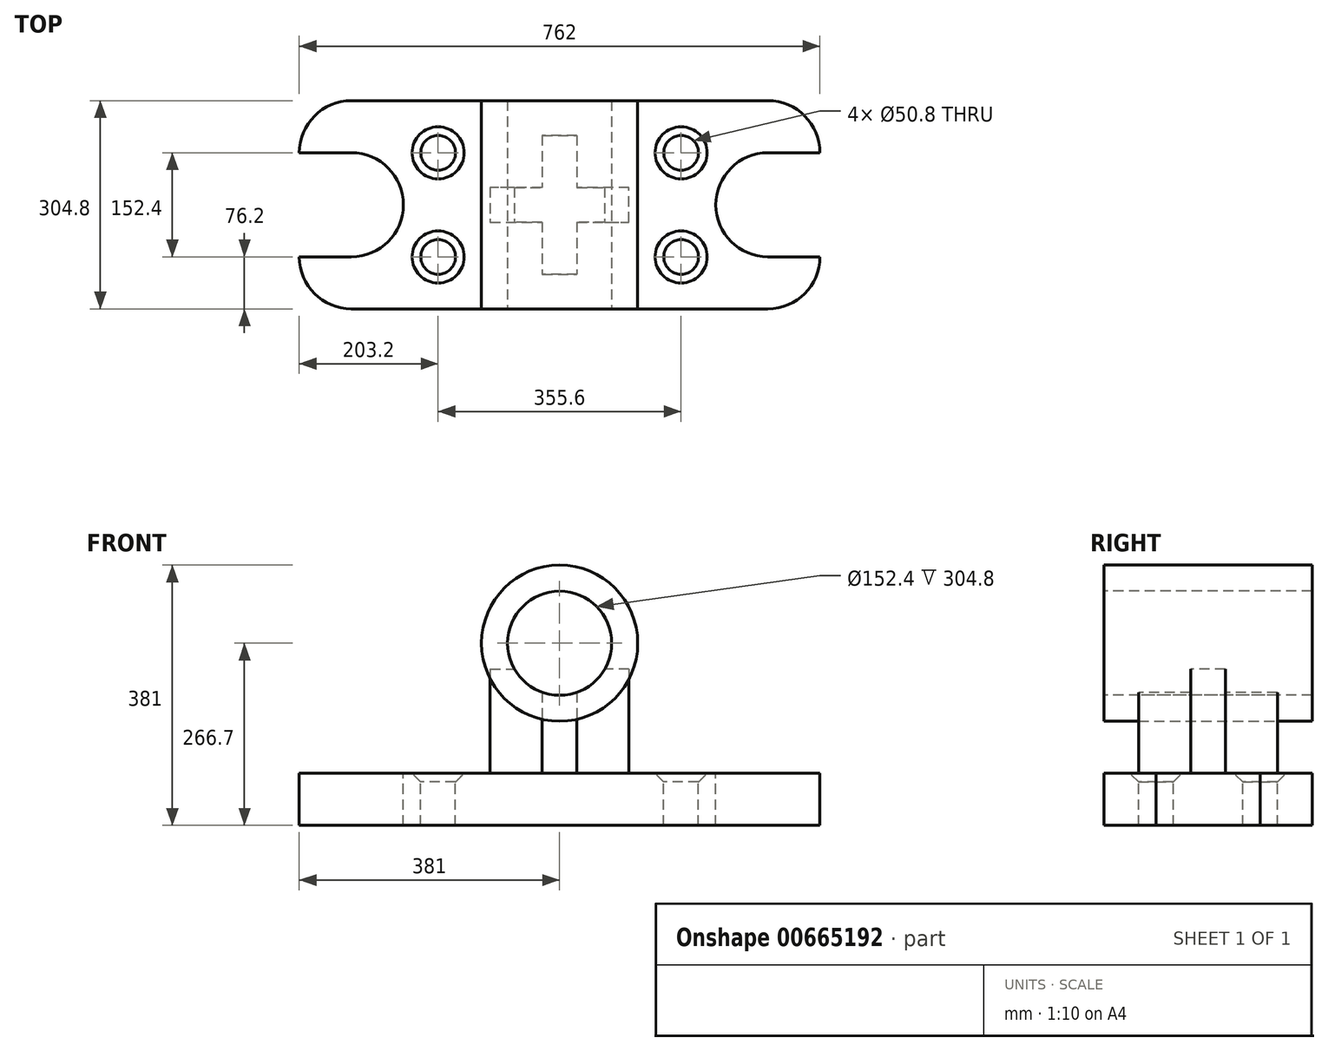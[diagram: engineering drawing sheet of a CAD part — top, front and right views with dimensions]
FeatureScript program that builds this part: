
annotation { "Feature Type Name" : "Feature", "Feature Type Description" : "" }
export const myFeature = defineFeature(function(context is Context, id is Id, definition is map)
    precondition{}
    {
        {
            var Q0;
            Q0=qCreatedBy(makeId("Top.planeOp"),FACE);
            var sketch = newSketch(context, id + "F0", { "sketchPlane" : qUnion([Q0])});
            skLineSegment(sketch, "E0.bottom", {"start": v(76.2, 0) * mm, "end": v(685.8, 0) * mm});
            skLineSegment(sketch, "E0.top", {"start": v(76.2, 304.8) * mm, "end": v(685.8, 304.8) * mm});
            skLineSegment(sketch, "E0.left", {"start": v(0, 76.2) * mm, "end": v(0, 228.6) * mm});
            skLineSegment(sketch, "E0.right", {"start": v(762, 76.2) * mm, "end": v(762, 228.6) * mm});
            skLineSegment(sketch, "E1", {"start": v(0, 228.6) * mm, "end": v(76.2, 228.6) * mm});
            skLineSegment(sketch, "E2", {"start": v(0, 76.2) * mm, "end": v(76.2, 76.2) * mm});
            skArc(sketch, "E3", {"start": v(76.2, 76.2) * mm, "mid": v(152.4, 152.4) * mm, "end": v(76.2, 228.6) * mm});
            skLineSegment(sketch, "E4", {"start": v(762, 228.6) * mm, "end": v(685.8, 228.6) * mm});
            skLineSegment(sketch, "E5", {"start": v(762, 76.2) * mm, "end": v(685.8, 76.2) * mm});
            skArc(sketch, "E6", {"start": v(685.8, 228.6) * mm, "mid": v(609.6, 152.4) * mm, "end": v(685.8, 76.2) * mm});
            skPoint(sketch, "E7.visualSharp", {"position": v(0, 304.8) * mm});
            skArc(sketch, "E7.filletArc", {"start": v(76.2, 304.8) * mm, "mid": v(22.32, 282.48) * mm, "end": v(0, 228.6) * mm});
            skPoint(sketch, "E8.visualSharp", {"position": v(762, 304.8) * mm});
            skArc(sketch, "E8.filletArc", {"start": v(762, 228.6) * mm, "mid": v(739.68, 282.48) * mm, "end": v(685.8, 304.8) * mm});
            skPoint(sketch, "E9.visualSharp", {"position": v(762, 0) * mm});
            skArc(sketch, "E9.filletArc", {"start": v(685.8, 0) * mm, "mid": v(739.68, 22.32) * mm, "end": v(762, 76.2) * mm});
            skPoint(sketch, "E10.visualSharp", {"position": v(0, 0) * mm});
            skArc(sketch, "E10.filletArc", {"start": v(0, 76.2) * mm, "mid": v(22.32, 22.32) * mm, "end": v(76.2, 0) * mm});
            skCircle(sketch, "E11", {"center": v(203.2, 228.6) * mm, "radius": 38.1 * mm});
            skCircle(sketch, "E12", {"center": v(203.2, 228.6) * mm, "radius": 25.4 * mm});
            skCircle(sketch, "E13", {"center": v(203.2, 76.2) * mm, "radius": 38.1 * mm});
            skCircle(sketch, "E14", {"center": v(203.2, 76.2) * mm, "radius": 25.4 * mm});
            skCircle(sketch, "E15", {"center": v(558.8, 76.2) * mm, "radius": 38.1 * mm});
            skCircle(sketch, "E16", {"center": v(558.8, 76.2) * mm, "radius": 25.4 * mm});
            skCircle(sketch, "E17", {"center": v(558.8, 228.6) * mm, "radius": 38.1 * mm});
            skCircle(sketch, "E18", {"center": v(558.8, 228.6) * mm, "radius": 25.4 * mm});
            skLineSegment(sketch, "E19", {"start": v(279.4, 177.8) * mm, "end": v(279.4, 127) * mm});
            skLineSegment(sketch, "E20", {"start": v(279.4, 127) * mm, "end": v(355.6, 127) * mm});
            skLineSegment(sketch, "E21", {"start": v(355.6, 127) * mm, "end": v(355.6, 50.8) * mm});
            skLineSegment(sketch, "E22", {"start": v(355.6, 50.8) * mm, "end": v(406.4, 50.8) * mm});
            skLineSegment(sketch, "E23", {"start": v(406.4, 50.8) * mm, "end": v(406.4, 127) * mm});
            skLineSegment(sketch, "E24", {"start": v(406.4, 127) * mm, "end": v(482.6, 127) * mm});
            skLineSegment(sketch, "E25", {"start": v(482.6, 127) * mm, "end": v(482.6, 177.8) * mm});
            skLineSegment(sketch, "E26", {"start": v(482.6, 177.8) * mm, "end": v(406.4, 177.8) * mm});
            skLineSegment(sketch, "E27", {"start": v(406.4, 177.8) * mm, "end": v(406.4, 254) * mm});
            skLineSegment(sketch, "E28", {"start": v(406.4, 254) * mm, "end": v(355.6, 254) * mm});
            skLineSegment(sketch, "E29", {"start": v(355.6, 254) * mm, "end": v(355.6, 177.8) * mm});
            skLineSegment(sketch, "E30", {"start": v(355.6, 177.8) * mm, "end": v(279.4, 177.8) * mm});
            skSolve(sketch);
        }
        {
            var Q0;
            Q0=makeQuery(id+"F0.imprint","IMPRINT",FACE,{"disambiguationData":[TD([[makeQuery(id+"F0.imprint","IMPRINT",EDGE,{"derivedFrom":sQuery(id+"F0.wireOp",EDGE,"E0.bottom")}),1.0]])]});
            var Q1;
            Q1=makeQuery(id+"F0.imprint","IMPRINT",FACE,{"disambiguationData":[TD([[makeQuery(id+"F0.imprint","IMPRINT",EDGE,{"derivedFrom":sQuery(id+"F0.wireOp",EDGE,"E19")}),1.0]])]});
            var Q2;
            Q2=makeQuery(id+"F0.imprint","IMPRINT",FACE,{"disambiguationData":[TD([[makeQuery(id+"F0.imprint","IMPRINT",EDGE,{"derivedFrom":sQuery(id+"F0.wireOp",EDGE,"E11")}),1.0]])]});
            var Q3;
            Q3=makeQuery(id+"F0.imprint","IMPRINT",FACE,{"disambiguationData":[TD([[makeQuery(id+"F0.imprint","IMPRINT",EDGE,{"derivedFrom":sQuery(id+"F0.wireOp",EDGE,"E13")}),1.0]])]});
            var Q4;
            Q4=makeQuery(id+"F0.imprint","IMPRINT",FACE,{"disambiguationData":[TD([[makeQuery(id+"F0.imprint","IMPRINT",EDGE,{"derivedFrom":sQuery(id+"F0.wireOp",EDGE,"E15")}),1.0]])]});
            var Q5;
            Q5=makeQuery(id+"F0.imprint","IMPRINT",FACE,{"disambiguationData":[TD([[makeQuery(id+"F0.imprint","IMPRINT",EDGE,{"derivedFrom":sQuery(id+"F0.wireOp",EDGE,"E17")}),1.0]])]});
            extrude(context, id + "F1", {"entities" : qUnion([Q0, Q1, Q2, Q3, Q4, Q5]), "oppositeDirection" : true, "depth" : 76.2 * mm, "offsetDistance" : 25.4 * mm});
        }
        {
            var Q0;
            Q0=makeQuery(id+"F1.opExtrude","CAP_EDGE",EDGE,{"disambiguationData":[OSD([sQuery(id+"F0.wireOp",EDGE,"E12")])],"isStart":true});
            var Q1;
            Q1=makeQuery(id+"F1.opExtrude","CAP_EDGE",EDGE,{"disambiguationData":[OSD([sQuery(id+"F0.wireOp",EDGE,"E14")])],"isStart":true});
            var Q2;
            Q2=makeQuery(id+"F1.opExtrude","CAP_EDGE",EDGE,{"disambiguationData":[OSD([sQuery(id+"F0.wireOp",EDGE,"E16")])],"isStart":true});
            var Q3;
            Q3=makeQuery(id+"F1.opExtrude","CAP_EDGE",EDGE,{"disambiguationData":[OSD([sQuery(id+"F0.wireOp",EDGE,"E18")])],"isStart":true});
            chamfer(context, id + "F2", {"entities" : qUnion([Q0, Q1, Q2, Q3]), "width" : 12.7 * mm, "tangentPropagation" : true});
        }
        {
            var Q0;
            Q0=makeQuery(id+"F1.opExtrude","SWEPT_FACE",FACE,{"disambiguationData":[OSD([sQuery(id+"F0.wireOp",EDGE,"E0.bottom")])]});
            cPlane(context, id + "F3", {"entities" : qUnion([Q0]), "cplaneType" : CPlaneType.OFFSET, "offset" : 152.4 * mm, "oppositeDirection" : true, "width" : 152.4 * mm, "height" : 152.4 * mm});
        }
        {
            var Q0;
            Q0=qCreatedBy(id+"F3.planeOp",FACE);
            var sketch = newSketch(context, id + "F4", { "sketchPlane" : qUnion([Q0])});
            skLineSegment(sketch, "E31", {"start": v(381, 76.2) * mm, "end": v(381, 190.5) * mm});
            skCircle(sketch, "E32", {"center": v(381, 190.5) * mm, "radius": 114.3 * mm});
            skSolve(sketch);
        }
        {
            var Q0;
            Q0=makeQuery(id+"F4.imprint","IMPRINT",FACE,{"disambiguationData":[TD([[makeQuery(id+"F4.imprint","IMPRINT",EDGE,{"derivedFrom":sQuery(id+"F4.wireOp",EDGE,"E32")}),1.0]])]});
            extrude(context, id + "F5", {"entities" : qUnion([Q0]), "endBound" : BoundingType.SYMMETRIC, "depth" : 304.8 * mm, "offsetDistance" : 25.4 * mm});
        }
        {
            var Q0;
            Q0=qCreatedBy(id+"F3.planeOp",FACE);
            var sketch = newSketch(context, id + "F6", { "sketchPlane" : qUnion([Q0])});
            skPoint(sketch, "E33", {"position": v(273.24, 152.4) * mm});
            skPoint(sketch, "E34", {"position": v(488.76, 152.4) * mm});
            skSolve(sketch);
        }
        {
            var Q0;
            Q0=makeQuery(id+"F5.opExtrude","CAP_FACE",FACE,{"disambiguationData":[OSD([sQuery(id+"F4.wireOp",EDGE,"E32")])],"isStart":false});
            var sketch = newSketch(context, id + "F7", { "sketchPlane" : qUnion([Q0])});
            skPoint(sketch, "E35", {"position": v(381, 190.5) * mm});
            skSolve(sketch);
        }
        {
            var Q0;
            Q0=makeQuery(id+"F0.imprint","IMPRINT",FACE,{"disambiguationData":[TD([[makeQuery(id+"F0.imprint","IMPRINT",EDGE,{"derivedFrom":sQuery(id+"F0.wireOp",EDGE,"E19")}),1.0]])]});
            var Q1;
            Q1=sQuery(id+"F6.wireOp",VERTEX,"E33");
            extrude(context, id + "F8", {"entities" : qUnion([Q0]), "endBound" : BoundingType.UP_TO_VERTEX, "depth" : 25.4 * mm, "endBoundEntityVertex" : qUnion([Q1]), "offsetDistance" : 25.4 * mm});
        }
        {
            var Q0;
            Q0=sQuery(id+"F7.wireOp",VERTEX,"E35");
            var Q1;
            Q1=makeQuery(id+"F5.opExtrude","SWEPT_BODY",BODY,{"disambiguationData":[OSD([sQuery(id+"F4.wireOp",EDGE,"E32")])]});
            var Q2;
            Q2=makeQuery(id+"F8.opExtrude","SWEPT_BODY",BODY,{"disambiguationData":[OSD([sQuery(id+"F0.wireOp",EDGE,"E19"),sQuery(id+"F0.wireOp",EDGE,"E20"),sQuery(id+"F0.wireOp",EDGE,"E21"),sQuery(id+"F0.wireOp",EDGE,"E22"),sQuery(id+"F0.wireOp",EDGE,"E23"),sQuery(id+"F0.wireOp",EDGE,"E24"),sQuery(id+"F0.wireOp",EDGE,"E25"),sQuery(id+"F0.wireOp",EDGE,"E26"),sQuery(id+"F0.wireOp",EDGE,"E27"),sQuery(id+"F0.wireOp",EDGE,"E28"),sQuery(id+"F0.wireOp",EDGE,"E29"),sQuery(id+"F0.wireOp",EDGE,"E30")])]});
            hole(context, id + "F9", {"style" : HoleStyle.SIMPLE, "endStyle" : HoleEndStyle.THROUGH, "holeDiameter" : 152.4 * mm, "majorDiameter" : 6.35 * mm, "isTappedThrough" : true, "tappedDepth" : 12.7 * mm, "tapClearance" : 3, "locations" : qUnion([Q0]), "scope" : qUnion([Q1, Q2])});
        }
    });
